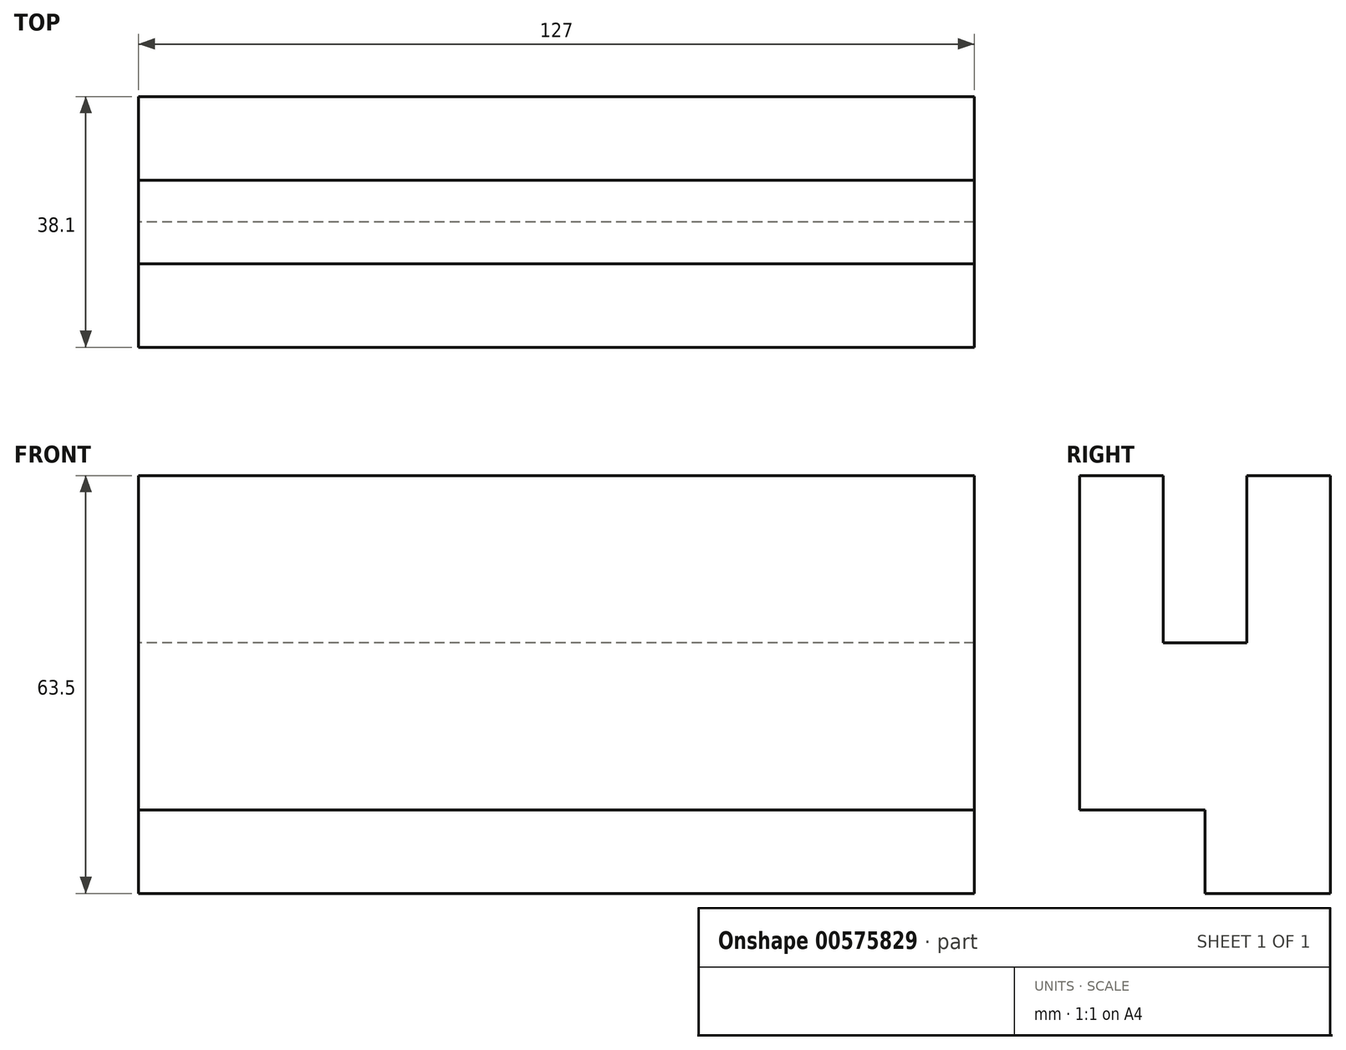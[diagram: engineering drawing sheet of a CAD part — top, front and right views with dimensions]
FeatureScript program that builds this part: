
annotation { "Feature Type Name" : "Feature", "Feature Type Description" : "" }
export const myFeature = defineFeature(function(context is Context, id is Id, definition is map)
    precondition{}
    {
        {
            var Q0;
            Q0=qCreatedBy(makeId("Right.planeOp"),FACE);
            var sketch = newSketch(context, id + "F0", { "sketchPlane" : qUnion([Q0])});
            skLineSegment(sketch, "E0", {"start": v(0, 0) * mm, "end": v(0, -50.8) * mm});
            skLineSegment(sketch, "E1", {"start": v(19.05, -63.5) * mm, "end": v(38.1, -63.5) * mm});
            skLineSegment(sketch, "E2", {"start": v(38.1, -63.5) * mm, "end": v(38.1, 0) * mm});
            skLineSegment(sketch, "E3", {"start": v(38.1, 0) * mm, "end": v(25.4, 0) * mm});
            skLineSegment(sketch, "E4", {"start": v(0, -50.8) * mm, "end": v(19.05, -50.8) * mm});
            skLineSegment(sketch, "E5", {"start": v(19.05, -50.8) * mm, "end": v(19.05, -63.5) * mm});
            skLineSegment(sketch, "E6", {"start": v(12.7, 0) * mm, "end": v(12.7, -25.4) * mm});
            skLineSegment(sketch, "E7", {"start": v(12.7, -25.4) * mm, "end": v(25.4, -25.4) * mm});
            skLineSegment(sketch, "E8", {"start": v(25.4, -25.4) * mm, "end": v(25.4, 0) * mm});
            skLineSegment(sketch, "E9.trimOffspring", {"start": v(12.7, 0) * mm, "end": v(0, 0) * mm});
            skPoint(sketch, "E10.orphan", {"position": v(0, -63.5) * mm});
            skSolve(sketch);
        }
        {
            var Q0;
            Q0 = qSketchRegion(id + "F0", true);
            extrude(context, id + "F1", {"entities" : qUnion([Q0]), "depth" : 127 * mm, "offsetDistance" : 25.4 * mm});
        }
    });
